# Revit family: Faucet-Wall_Mount-Kitchen-KOHLER-Kumin-K-99483IN_1
name_source: partatom
category: Plumbing Fixtures
units: mm (PartAtom-declared; Revit-internal decimal feet)

## family parameters
Cut with Voids When Loaded = No
Host = Face
Maintain Annotation Orientation = No
OmniClass Number = 23.31.11.00
OmniClass Title = Faucets
Part Type = Normal
Room Calculation Point = No
Round Connector Dimension = Use Diameter
Shared = No

## types (2) — shared parameters
ADA Compliant = No
Assembly Code = D2010
CW Connection = Yes
Cold Water Inlet = Cold Water Inlet
Date Modified = 02/16/2022
Default Elevation = 36"
Drain Included = No
Finish = Kohler-Metal-CP-Polished_Chrome
Flow Rate = 10 GPM
HW Connection = Yes
Handle Clearance = 3 1/4"
Height = 9 5/8"
Hot Water Inlet = Hot Water Inlet
Length = 9 11/16"
Manufacturer = KOHLER Co.
Master Format 2014 = 22 41 39
Master Format 2014 Name = Residential Faucets, Supplies, and Trim
Material = Premium Metal Construction
Pressure = 43.50 psi
Product Name = KUMIN
Spout Reach = 9 11/16"
URL = https://www.kohler.co.in
Vent Connection = No
Waste Connection = No
Waste Water Outlet = Waste Water Outlet
WaterSense Certified = No
Width = 5 7/8"

## per-type parameters (varying)
| type | Description | Model | Premium Faucet | Product Page URL | Type | _4 |
| CP-Polished Chrome | WALL MOUNT KITCHEN FAUCET | K-99483IN-4-CP | No |  | 1 | Yes |
| Premium Faucet, CP-Polished Chrome | Single-handle Wall Mount Kitchen Faucet In Polished Chrome | K-99483IN-A4-CP | Yes | https://www.kohler.co.in | 2 | No |

## geometry (parser evidence)
native form markers: Sweep x4
no freeform markers — native parametric forms only
